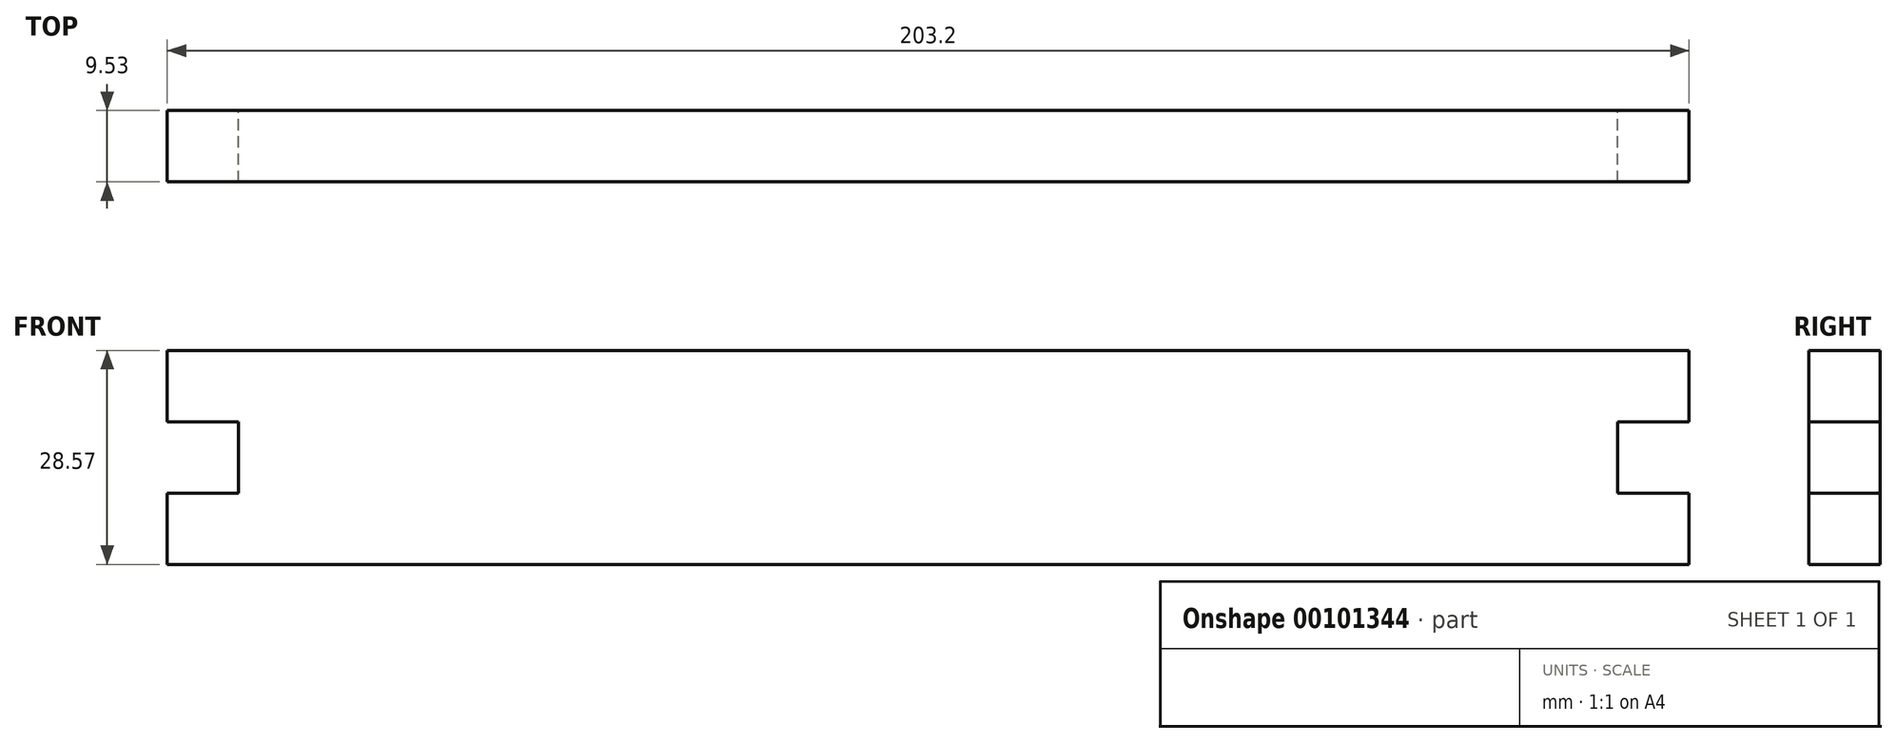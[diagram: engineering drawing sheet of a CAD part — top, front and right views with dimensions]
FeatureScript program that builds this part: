
annotation { "Feature Type Name" : "Feature", "Feature Type Description" : "" }
export const myFeature = defineFeature(function(context is Context, id is Id, definition is map)
    precondition{}
    {
        {
            var Q0;
            Q0=qCreatedBy(makeId("Front.planeOp"),FACE);
            var sketch = newSketch(context, id + "F0", { "sketchPlane" : qUnion([Q0])});
            skLineSegment(sketch, "E0.bottom", {"start": v(0, 0) * mm, "end": v(203.2, 0) * mm});
            skLineSegment(sketch, "E0.top", {"start": v(0, 28.58) * mm, "end": v(203.2, 28.58) * mm});
            skLineSegment(sketch, "E0.left", {"start": v(0, 0) * mm, "end": v(0, 28.58) * mm});
            skLineSegment(sketch, "E0.right", {"start": v(203.2, 0) * mm, "end": v(203.2, 28.58) * mm});
            skSolve(sketch);
        }
        {
            var Q0;
            Q0 = qSketchRegion(id + "F0", true);
            extrude(context, id + "F1", {"entities" : qUnion([Q0]), "depth" : 9.52 * mm});
        }
        {
            var Q0;
            Q0=qCreatedBy(makeId("Front.planeOp"),FACE);
            var sketch = newSketch(context, id + "F2", { "sketchPlane" : qUnion([Q0])});
            skLineSegment(sketch, "E1.bottom", {"start": v(0, 19.05) * mm, "end": v(9.53, 19.05) * mm});
            skLineSegment(sketch, "E1.top", {"start": v(0, 9.53) * mm, "end": v(9.53, 9.53) * mm});
            skLineSegment(sketch, "E1.left", {"start": v(0, 19.05) * mm, "end": v(0, 9.53) * mm});
            skLineSegment(sketch, "E1.right", {"start": v(9.53, 19.05) * mm, "end": v(9.53, 9.53) * mm});
            skLineSegment(sketch, "E2", {"start": v(0, 9.53) * mm, "end": v(0, 0) * mm});
            skLineSegment(sketch, "E3", {"start": v(101.6, 0) * mm, "end": v(101.6, 28.58) * mm});
            skLineSegment(sketch, "E4.MirrorCS", {"start": v(203.2, 9.53) * mm, "end": v(203.2, 0) * mm});
            skLineSegment(sketch, "E5.MirrorCS", {"start": v(193.68, 19.05) * mm, "end": v(193.68, 9.53) * mm});
            skLineSegment(sketch, "E6.MirrorCS", {"start": v(203.2, 19.05) * mm, "end": v(203.2, 9.53) * mm});
            skLineSegment(sketch, "E7.MirrorCS", {"start": v(203.2, 19.05) * mm, "end": v(193.68, 19.05) * mm});
            skLineSegment(sketch, "E8.MirrorCS", {"start": v(203.2, 9.53) * mm, "end": v(193.68, 9.53) * mm});
            skSolve(sketch);
        }
        {
            var Q0;
            Q0 = qSketchRegion(id + "F2", true);
            extrude(context, id + "F3", {"entities" : qUnion([Q0]), "operationType" : NewBodyOperationType.REMOVE, "endBound" : BoundingType.UP_TO_NEXT, "depth" : 25.4 * mm});
        }
    });
